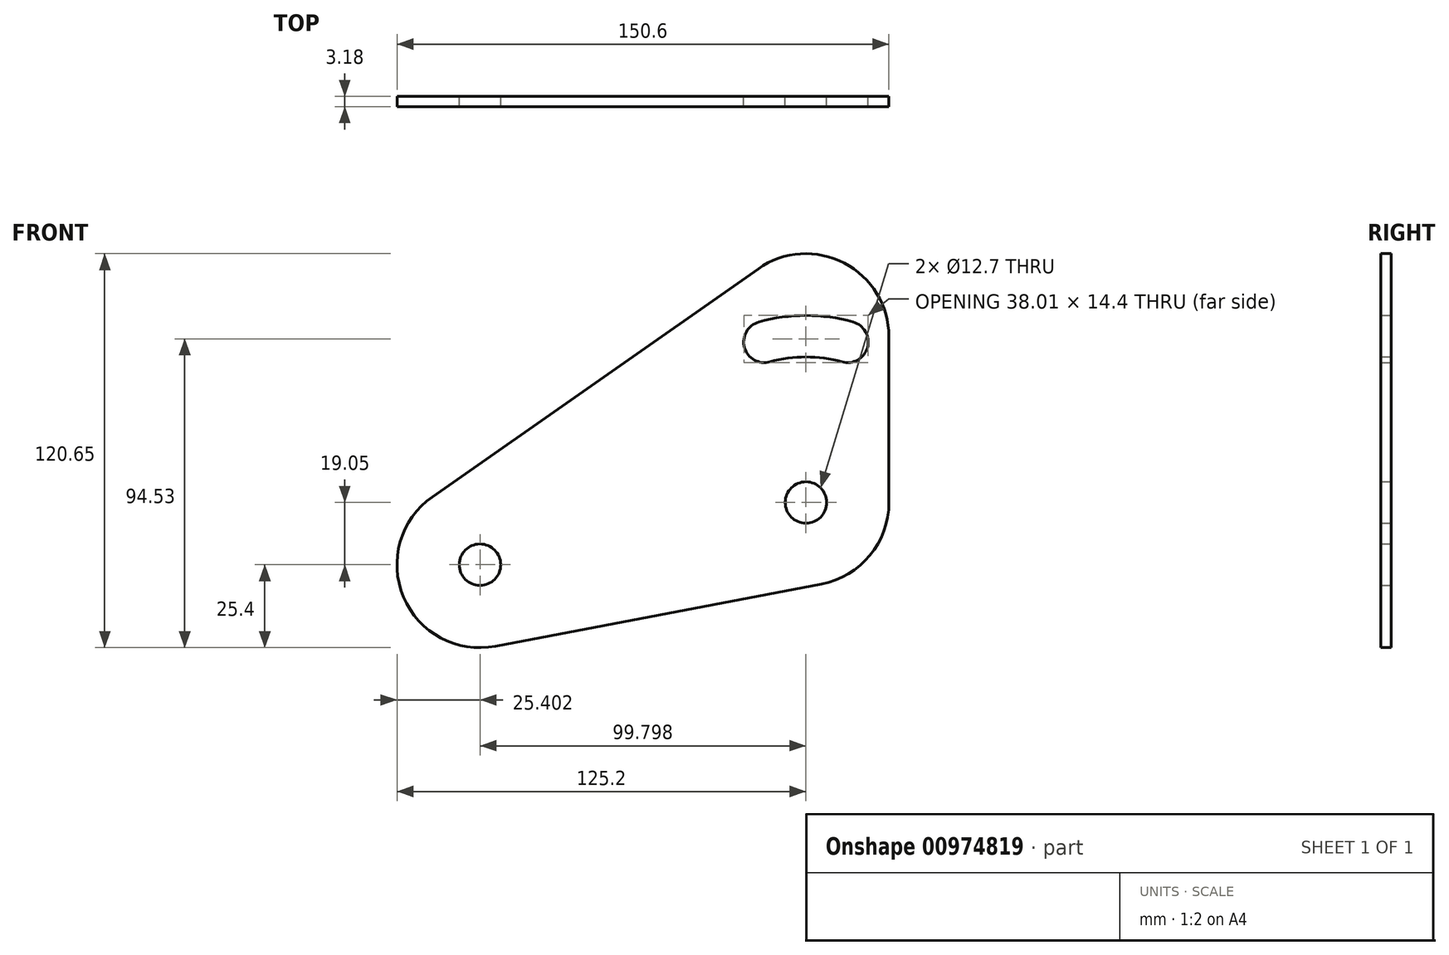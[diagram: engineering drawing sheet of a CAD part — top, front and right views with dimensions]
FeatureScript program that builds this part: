
annotation { "Feature Type Name" : "Feature", "Feature Type Description" : "" }
export const myFeature = defineFeature(function(context is Context, id is Id, definition is map)
    precondition{}
    {
        {
            var Q0;
            Q0=qCreatedBy(makeId("Front.planeOp"),FACE);
            var sketch = newSketch(context, id + "F0", { "sketchPlane" : qUnion([Q0])});
            skCircle(sketch, "E0", {"center": v(0, 0) * mm, "radius": 25.4 * mm});
            skCircle(sketch, "E1", {"center": v(0, 0) * mm, "radius": 6.35 * mm});
            skCircle(sketch, "E2", {"center": v(-99.8, -19.05) * mm, "radius": 6.35 * mm});
            skCircle(sketch, "E3", {"center": v(-99.8, -19.05) * mm, "radius": 25.4 * mm});
            skCircle(sketch, "E4", {"center": v(0, 50.8) * mm, "radius": 25.4 * mm});
            skLineSegment(sketch, "E5", {"start": v(-114.36, 1.76) * mm, "end": v(-14.56, 71.6) * mm});
            skLineSegment(sketch, "E6", {"start": v(25.4, 50.8) * mm, "end": v(25.4, 0) * mm});
            skLineSegment(sketch, "E7", {"start": v(4.76, -24.95) * mm, "end": v(-95.04, -44) * mm});
            skArc(sketch, "E8", {"start": v(-12.7, 49.19) * mm, "mid": v(0, 50.8) * mm, "end": v(12.7, 49.19) * mm, "construction": true});
            skCircle(sketch, "E9", {"center": v(-12.7, 49.19) * mm, "radius": 6.35 * mm});
            skCircle(sketch, "E10", {"center": v(12.7, 49.19) * mm, "radius": 6.35 * mm});
            skArc(sketch, "E11", {"start": v(14.4, 55.3) * mm, "mid": v(0, 57.28) * mm, "end": v(-14.4, 55.3) * mm});
            skArc(sketch, "E12", {"start": v(11, 43.07) * mm, "mid": v(0, 44.58) * mm, "end": v(-11, 43.07) * mm});
            skSolve(sketch);
        }
        {
            var Q0;
            Q0 = qSketchRegion(id + "F0", true);
            extrude(context, id + "F1", {"entities" : qUnion([Q0]), "depth" : 3.17 * mm, "offsetDistance" : 25.4 * mm});
        }
    });
